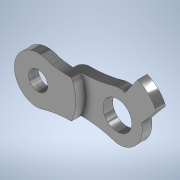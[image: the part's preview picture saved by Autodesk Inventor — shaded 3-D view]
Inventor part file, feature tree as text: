
AUTODESK INVENTOR PART (.ipt)
format: ipt  version: 2021 (Build 250183000, 183)  size: 165,376 bytes
history: native  units: in
note: dims shown in document units (in); Inventor stores cm internally (conversion verified against a paired STEP export)
features: extrude x4, sketch x2, fillet x1
ambient origin geometry x8: Origin, YZ Plane, XZ Plane, XY Plane, X Axis, Y Axis, Z Axis, Center Point
bodies: Solid1 (feature_tree)
feature tree (7):
  sketch  "Sketch1"  dims[d0=0.1969in d1=0.4724in]
  extrude  "Extrusion1"  Depth=0.4724in
  extrude  "Extrusion2"  Depth=0.0276in
  extrude  "Extrusion3"  Depth=0.0276in
  extrude  "Extrusão4"  Depth=0.0276in
  fillet  "Arredondamento1"  Radius=0.1181in
  sketch  "Esboço2"  dims[d2=0.0787in d3=0.0787in d5=0.0787in d6=0.0787in d7=0.1181in d8=0.0591in d9=0.0512in d10=0.0394in d11=0.0in d12=0.0394in d13=0.0in d14=0.0394in d15=0.0in d16=0.0394in d17=0.0in d18=0.0276in]
